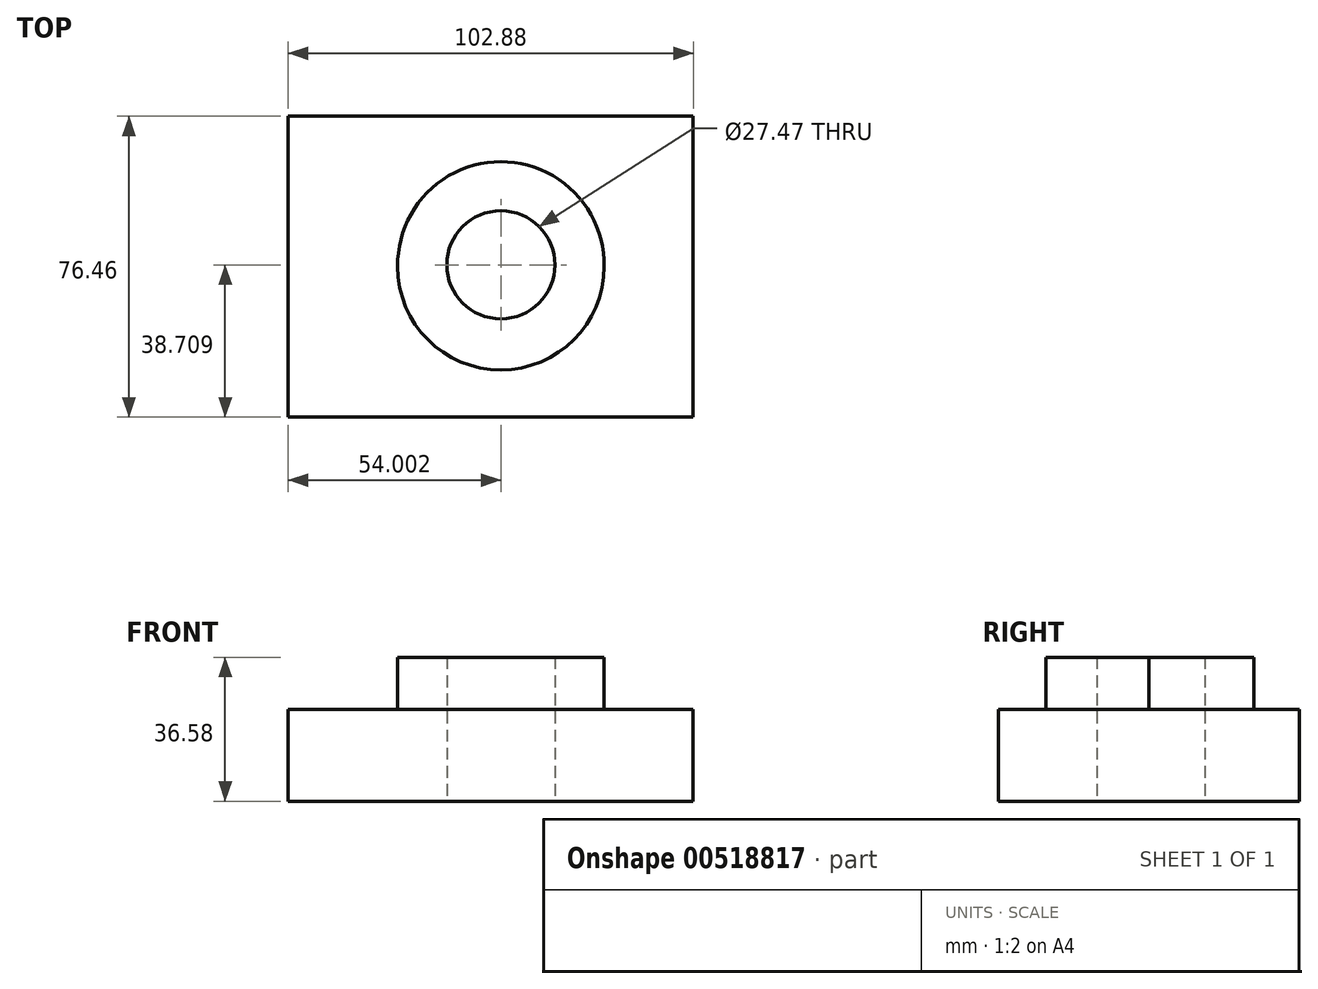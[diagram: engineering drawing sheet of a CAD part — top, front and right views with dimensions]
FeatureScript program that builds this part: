
annotation { "Feature Type Name" : "Feature", "Feature Type Description" : "" }
export const myFeature = defineFeature(function(context is Context, id is Id, definition is map)
    precondition{}
    {
        {
            var Q0;
            Q0=qCreatedBy(makeId("Top.planeOp"),FACE);
            var sketch = newSketch(context, id + "F0", { "sketchPlane" : qUnion([Q0])});
            skLineSegment(sketch, "E0.bottom", {"start": v(-51.44, 38.23) * mm, "end": v(51.44, 38.23) * mm});
            skLineSegment(sketch, "E0.top", {"start": v(-51.44, -38.23) * mm, "end": v(51.44, -38.23) * mm});
            skLineSegment(sketch, "E0.left", {"start": v(-51.44, 38.23) * mm, "end": v(-51.44, -38.23) * mm});
            skLineSegment(sketch, "E0.right", {"start": v(51.44, 38.23) * mm, "end": v(51.44, -38.23) * mm});
            skPoint(sketch, "E0.middle", {"position": v(0, 0) * mm});
            skArc(sketch, "E1", {"start": v(-23.65, 0) * mm, "mid": v(2.56, -26.21) * mm, "end": v(28.77, 0) * mm});
            skArc(sketch, "E2", {"start": v(28.77, 0) * mm, "mid": v(2.56, 26.7) * mm, "end": v(-23.65, 0) * mm});
            skCircle(sketch, "E3", {"center": v(2.56, 0.48) * mm, "radius": 13.73 * mm});
            skSolve(sketch);
        }
        {
            var Q0;
            Q0=makeQuery(id+"F0.imprint","IMPRINT",FACE,{"disambiguationData":[TD([[makeQuery(id+"F0.imprint","IMPRINT",EDGE,{"derivedFrom":sQuery(id+"F0.wireOp",EDGE,"E1")}),1.0]])]});
            extrude(context, id + "F1", {"entities" : qUnion([Q0]), "depth" : 36.58 * mm, "offsetDistance" : 25.4 * mm});
        }
        {
            var Q0;
            Q0=makeQuery(id+"F0.imprint","IMPRINT",FACE,{"disambiguationData":[TD([[makeQuery(id+"F0.imprint","IMPRINT",EDGE,{"derivedFrom":sQuery(id+"F0.wireOp",EDGE,"E0.bottom")}),-1.0]])]});
            extrude(context, id + "F2", {"entities" : qUnion([Q0]), "operationType" : NewBodyOperationType.ADD, "depth" : 23.37 * mm, "offsetDistance" : 25.4 * mm});
        }
    });
